# Revit family: Aircom Supra Circular
name_source: partatom
category: Luminarias
revit_build: Autodesk Revit 2015 (Build: 20140606_1530(x64)
units: mm (PartAtom-declared; Revit-internal decimal feet)

## types (4) — shared parameters
Cambio de temperatura de color de luz atenuada = <Ninguno>
Diametro = 213 mm  [stored 0.698819 ft]
Diametro de corte = 195 mm  [stored 0.639764 ft]
Diámetro de círculo de emisión = 176 mm  [stored 0.577428 ft]
Fabricante = SECOM ILUMINACIÓN
Filtro de color = 16777215
Forma visible en renderización = No
Lámpara = LED Osram Duris E5
Modelo = Aircom Supra Circular
longitud = 83 mm  [stored 0.27231 ft]
Ángulo de inclinación = 90.00°

## per-type parameters (varying)
| type | Archivo de red fotométrica | Descripción |
| Aircom Supra Circular 20W | 4227 01 20 84 MATE.IES | 4227 01 20 84 |
| Aircom Supra Circular 30W | 4227 01 30 84 MATE.IES | 4227 01 30 84 |
| Aircom Supra Circular 40W | 4227 01 40 84 MATE.IES | 4227 01 40 84 |
| Aircom Supra Circular 60W | 4227 01 60 84 MATE.IES | 4227 01 60 84 |

note: [stored X ft] marks values corroborated as IEEE doubles in the binary element streams (Revit-internal decimal feet)
